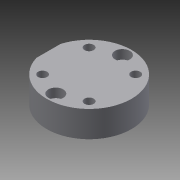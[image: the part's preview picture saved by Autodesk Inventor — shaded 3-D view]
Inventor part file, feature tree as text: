
AUTODESK INVENTOR PART (.ipt)
format: ipt  version: 2014 SP2 (Build 180246200, 246)  size: 247,808 bytes
history: native  units: in
note: dims shown in document units (in); Inventor stores cm internally (conversion verified against a paired STEP export)
features: other x259, sketch x7, hole x4, revolve x2, extrude x1, thread x1, pattern_linear x1
ambient origin geometry x8: Origin, YZ Plane, XZ Plane, XY Plane, X Axis, Y Axis, Z Axis, Center Point
bodies: Solid1 (feature_tree)
feature tree (275):
  revolve  "Revolution1"  [1 undecoded]
  extrude  "Extrusion1"  Depth=0.1831in TaperAngle=0.0deg
  revolve  "Revolution2"  [1 undecoded]
  thread  "Thread1"  [1 undecoded]
  hole  "Hole1"  [1 undecoded]
  hole  "Hole2"  [1 undecoded]
  hole  "Hole3"  [1 undecoded]
  hole  "Hole4"  [1 undecoded]
  pattern_linear  "Rectangular Pattern1"  [2 undecoded]
  other  "a1_XY"
  other  "a1_YZ"
  other  "a1_ZX"
  other  "a1_X"
  other  "a1_Y"
  other  "a1_Z"
  other  "a1_Center"
  other  "a2_XY"
  other  "a2_YZ"
  other  "a2_ZX"
  other  "a2_X"
  other  "a2_Y"
  other  "a2_Z"
  other  "a2_Center"
  other  "ar3_XY"
  other  "ar3_YZ"
  other  "ar3_ZX"
  other  "ar3_X"
  other  "ar3_Y"
  other  "ar3_Z"
  other  "ar3_Center"
  other  "ar4_XY"
  other  "ar4_YZ"
  other  "ar4_ZX"
  other  "ar4_X"
  other  "ar4_Y"
  other  "ar4_Z"
  other  "ar4_Center"
  other  "ar5_XY"
  other  "ar5_YZ"
  other  "ar5_ZX"
  other  "ar5_X"
  other  "ar5_Y"
  other  "ar5_Z"
  other  "ar5_Center"
  other  "ar6_XY"
  other  "ar6_YZ"
  other  "ar6_ZX"
  other  "ar6_X"
  other  "ar6_Y"
  other  "ar6_Z"
  other  "ar6_Center"
  other  "b1_XY"
  other  "b1_YZ"
  other  "b1_ZX"
  other  "b1_X"
  other  "b1_Y"
  other  "b1_Z"
  other  "b1_Center"
  other  "j_XY"
  other  "j_YZ"
  other  "j_ZX"
  other  "j_X"
  other  "j_Y"
  other  "j_Z"
  other  "j_Center"
  other  "k1_XY"
  other  "k1_YZ"
  other  "k1_ZX"
  other  "k1_X"
  other  "k1_Y"
  other  "k1_Z"
  other  "k1_Center"
  other  "k2_XY"
  other  "k2_YZ"
  other  "k2_ZX"
  other  "k2_X"
  other  "k2_Y"
  other  "k2_Z"
  other  "k2_Center"
  other  "l1_XY"
  other  "l1_YZ"
  other  "l1_ZX"
  other  "l1_X"
  other  "l1_Y"
  other  "l1_Z"
  other  "l1_Center"
  other  "l2_XY"
  other  "l2_YZ"
  other  "l2_ZX"
  other  "l2_X"
  other  "l2_Y"
  other  "l2_Z"
  other  "l2_Center"
  other  "po1_XY"
  other  "po1_YZ"
  other  "po1_ZX"
  other  "po1_X"
  other  "po1_Y"
  other  "po1_Z"
  other  "po1_Center"
  other  "po2_XY"
  other  "po2_YZ"
  other  "po2_ZX"
  other  "po2_X"
  other  "po2_Y"
  other  "po2_Z"
  other  "po2_Center"
  other  "po3_XY"
  other  "po3_YZ"
  other  "po3_ZX"
  other  "po3_X"
  other  "po3_Y"
  other  "po3_Z"
  other  "po3_Center"
  other  "r7_XY"
  other  "r7_YZ"
  other  "r7_ZX"
  other  "r7_X"
  other  "r7_Y"
  other  "r7_Z"
  other  "r7_Center"
  other  "r71_XY"
  other  "r71_YZ"
  other  "r71_ZX"
  other  "r71_X"
  other  "r71_Y"
  other  "r71_Z"
  other  "r71_Center"
  other  "r72_XY"
  other  "r72_YZ"
  other  "r72_ZX"
  other  "r72_X"
  other  "r72_Y"
  other  "r72_Z"
  other  "r72_Center"
  other  "r73_XY"
  other  "r73_YZ"
  other  "r73_ZX"
  other  "r73_X"
  other  "r73_Y"
  other  "r73_Z"
  other  "r73_Center"
  other  "rg_XY"
  other  "rg_YZ"
  other  "rg_ZX"
  other  "rg_X"
  other  "rg_Y"
  other  "rg_Z"
  other  "rg_Center"
  other  "rh_XY"
  other  "rh_YZ"
  other  "rh_ZX"
  other  "rh_X"
  other  "rh_Y"
  other  "rh_Z"
  other  "rh_Center"
  other  "rs_1_XY"
  other  "rs_1_YZ"
  other  "rs_1_ZX"
  other  "rs_1_X"
  other  "rs_1_Y"
  other  "rs_1_Z"
  other  "rs_1_Center"
  other  "rs_2_XY"
  other  "rs_2_YZ"
  other  "rs_2_ZX"
  other  "rs_2_X"
  other  "rs_2_Y"
  other  "rs_2_Z"
  other  "rs_2_Center"
  other  "rs_3_XY"
  other  "rs_3_YZ"
  other  "rs_3_ZX"
  other  "rs_3_X"
  other  "rs_3_Y"
  other  "rs_3_Z"
  other  "rs_3_Center"
  other  "rs_4_XY"
  other  "rs_4_YZ"
  other  "rs_4_ZX"
  other  "rs_4_X"
  other  "rs_4_Y"
  other  "rs_4_Z"
  other  "rs_4_Center"
  other  "sc1_XY"
  other  "sc1_YZ"
  other  "sc1_ZX"
  other  "sc1_X"
  other  "sc1_Y"
  other  "sc1_Z"
  other  "sc1_Center"
  other  "sc2_XY"
  other  "sc2_YZ"
  other  "sc2_ZX"
  other  "sc2_X"
  other  "sc2_Y"
  other  "sc2_Z"
  other  "sc2_Center"
  other  "sc3_XY"
  other  "sc3_YZ"
  other  "sc3_ZX"
  other  "sc3_X"
  other  "sc3_Y"
  other  "sc3_Z"
  other  "sc3_Center"
  other  "to_dummy_XY"
  other  "to_dummy_YZ"
  other  "to_dummy_ZX"
  other  "to_dummy_X"
  other  "to_dummy_Y"
  other  "to_dummy_Z"
  other  "to_dummy_Center"
  other  "to_nut_XY"
  other  "to_nut_YZ"
  other  "to_nut_ZX"
  other  "to_nut_X"
  other  "to_nut_Y"
  other  "to_nut_Z"
  other  "to_nut_Center"
  other  "to_rod_XY"
  other  "to_rod_YZ"
  other  "to_rod_ZX"
  other  "to_rod_X"
  other  "to_rod_Y"
  other  "to_rod_Z"
  other  "to_rod_Center"
  other  "to_tube_XY"
  other  "to_tube_YZ"
  other  "to_tube_ZX"
  other  "to_tube_X"
  other  "to_tube_Y"
  other  "to_tube_Z"
  other  "to_tube_Center"
  other  "to_wiper_XY"
  other  "to_wiper_YZ"
  other  "to_wiper_ZX"
  other  "to_wiper_X"
  other  "to_wiper_Y"
  other  "to_wiper_Z"
  other  "to_wiper_Center"
  other  "track1_XY"
  other  "track1_YZ"
  other  "track1_ZX"
  other  "track1_X"
  other  "track1_Y"
  other  "track1_Z"
  other  "track1_Center"
  other  "track2_XY"
  other  "track2_YZ"
  other  "track2_ZX"
  other  "track2_X"
  other  "track2_Y"
  other  "track2_Z"
  other  "track2_Center"
  other  "track3_XY"
  other  "track3_YZ"
  other  "track3_ZX"
  other  "track3_X"
  other  "track3_Y"
  other  "track3_Z"
  other  "track3_Center"
  other  "track4_XY"
  other  "track4_YZ"
  other  "track4_ZX"
  other  "track4_X"
  other  "track4_Y"
  other  "track4_Z"
  other  "track4_Center"
  sketch  "Sketch_1"  dims[d0=360.0deg d1=0.344in d2=0.0in]
  sketch  "Sketch_63"  dims[d40=0.0in d41=0.0in d42=0.0in d43=0.0in d44=0.0in d45=0.0in d46=0.0in d47=0.0in d48=0.0in d49=0.0in d50=0.0in d51=0.0in d52=0.0in d53=0.0in d54=0.0in d55=0.0in d56=0.0in d57=0.0in d58=0.0in d59=0.0in d60=0.0in]
  sketch  "Sketch_37"  dims[d27=0.0849in d28=0.344in d29=0.12in d30=0.1in d31=0.5635in d32=0.344in d33=0.0in d34=0.7874in d36=0.6109in d37=0.7874in d39=0.6109in]
  sketch  "Sketch4"  dims[d3=360.0deg d4=0.1831in d5=0.0in]
  sketch  "Sketch5"  dims[d6=0.61in d7=0.75in d8=0.375in d9=0.25in d10=0.5635in d11=0.1in d12=0.0in]
  sketch  "Sketch6"  dims[d13=0.1285in d14=0.75in d15=0.195in d16=0.12in d17=0.5635in d18=0.344in d19=0.0in]
  sketch  "Sketch7"  dims[d20=0.1285in d21=0.75in d22=0.195in d23=0.12in d24=0.5635in d25=0.344in d26=0.0in]
note: 9 required parameter values undecoded (feature->parameter linkage not recoverable at this tier; creation-order binding heuristic only, values carry confidence <= 0.55)